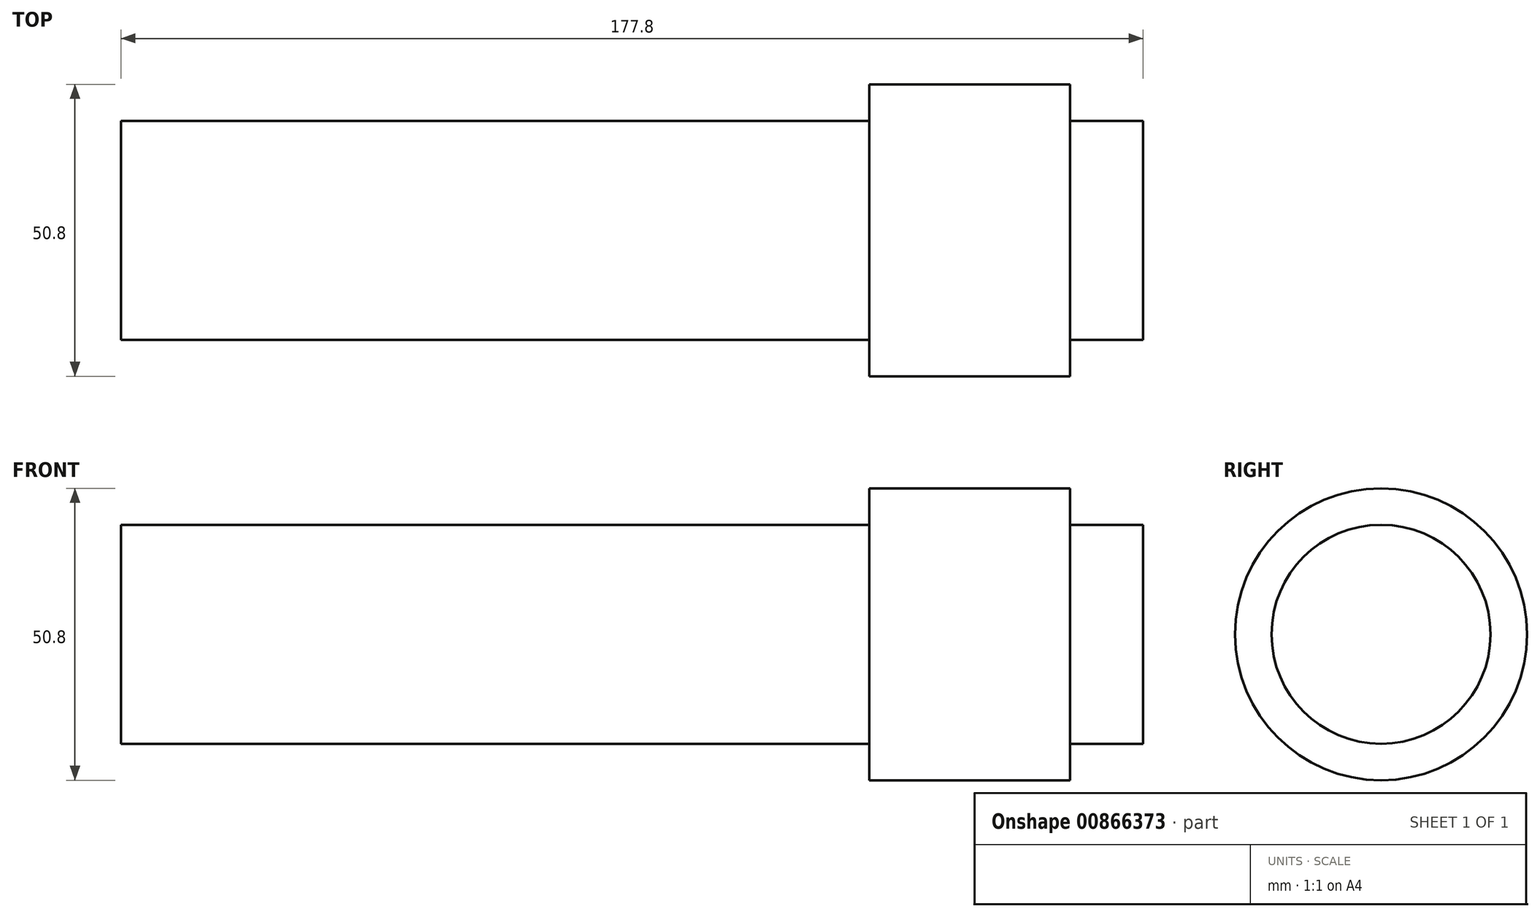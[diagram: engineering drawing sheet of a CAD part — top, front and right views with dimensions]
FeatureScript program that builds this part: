
annotation { "Feature Type Name" : "Feature", "Feature Type Description" : "" }
export const myFeature = defineFeature(function(context is Context, id is Id, definition is map)
    precondition{}
    {
        {
            var Q0;
            Q0=qCreatedBy(makeId("Front.planeOp"),FACE);
            var sketch = newSketch(context, id + "F0", { "sketchPlane" : qUnion([Q0])});
            skLineSegment(sketch, "E0", {"start": v(-73.14, 0) * mm, "end": v(-73.14, 19.05) * mm});
            skLineSegment(sketch, "E1", {"start": v(-73.14, 19.05) * mm, "end": v(57.03, 19.05) * mm});
            skLineSegment(sketch, "E2", {"start": v(57.03, 19.05) * mm, "end": v(57.03, 25.4) * mm});
            skLineSegment(sketch, "E3", {"start": v(57.03, 25.4) * mm, "end": v(91.96, 25.4) * mm});
            skLineSegment(sketch, "E4", {"start": v(91.96, 25.4) * mm, "end": v(91.96, 19.05) * mm});
            skLineSegment(sketch, "E5", {"start": v(91.96, 19.05) * mm, "end": v(104.66, 19.05) * mm});
            skLineSegment(sketch, "E6", {"start": v(104.66, 19.05) * mm, "end": v(104.66, 0) * mm});
            skLineSegment(sketch, "E7", {"start": v(-73.14, 0) * mm, "end": v(104.66, 0) * mm});
            skSolve(sketch);
        }
        {
            var Q0;
            Q0=makeQuery(id+"F0.imprint","IMPRINT",FACE,{"disambiguationData":[TD([[makeQuery(id+"F0.imprint","IMPRINT",EDGE,{"derivedFrom":sQuery(id+"F0.wireOp",EDGE,"E0")}),-1.0]])]});
            var Q1;
            Q1=sQuery(id+"F0.wireOp",EDGE,"E7");
            revolve(context, id + "F1", {"surfaceOperationType" : NewSurfaceOperationType.NEW, "entities" : qUnion([Q0]), "axis" : qUnion([Q1]), "revolveType" : RevolveType.FULL});
        }
    });
